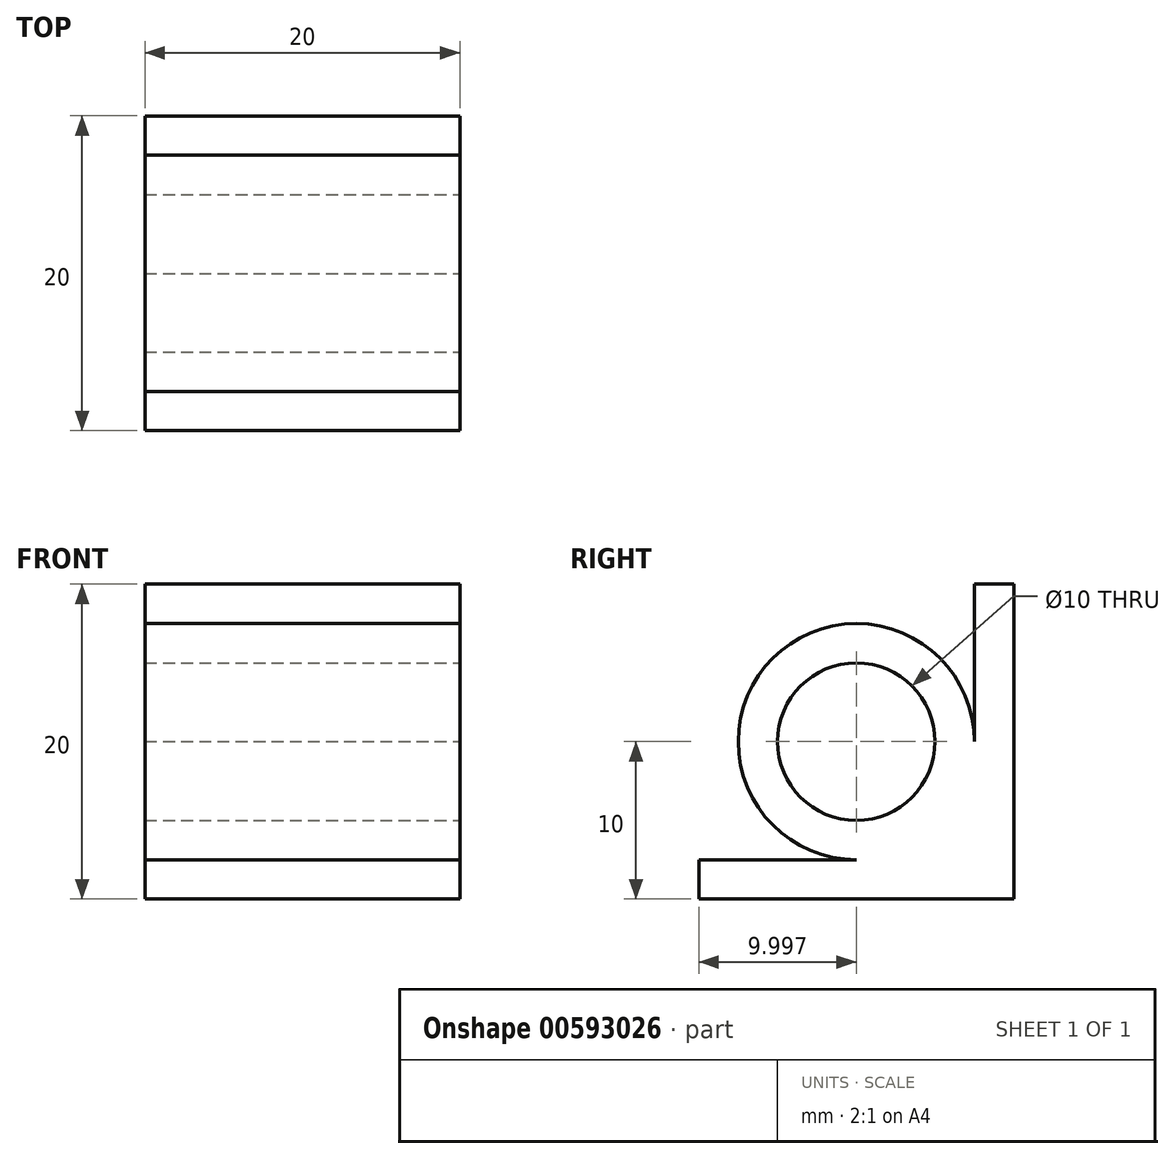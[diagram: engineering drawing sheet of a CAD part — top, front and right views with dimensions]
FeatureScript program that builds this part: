
annotation { "Feature Type Name" : "Feature", "Feature Type Description" : "" }
export const myFeature = defineFeature(function(context is Context, id is Id, definition is map)
    precondition{}
    {
        {
            var Q0;
            Q0=qCreatedBy(makeId("Top.planeOp"),FACE);
            var sketch = newSketch(context, id + "F0", { "sketchPlane" : qUnion([Q0])});
            skLineSegment(sketch, "E0", {"start": v(-97.21, -75.5) * mm, "end": v(-97.21, -55.5) * mm});
            skLineSegment(sketch, "E1", {"start": v(-97.21, -75.5) * mm, "end": v(-77.21, -75.5) * mm});
            skLineSegment(sketch, "E2", {"start": v(-77.21, -75.5) * mm, "end": v(-77.21, -55.5) * mm});
            skLineSegment(sketch, "E3", {"start": v(-77.21, -55.5) * mm, "end": v(-97.21, -55.5) * mm});
            skSolve(sketch);
        }
        {
            var Q0;
            Q0 = qSketchRegion(id + "F0", true);
            var Q1;
            Q1 = qSketchRegion(id + "F3", true);
            var Q2;
            Q2 = qSketchRegion(id + "F2", true);
            extrude(context, id + "F1", {"entities" : qUnion([Q0, Q1, Q2]), "depth" : 20 * mm, "offsetDistance" : 25 * mm});
        }
        {
            var Q0;
            Q0=qCreatedBy(makeId("Top.planeOp"),FACE);
            var sketch = newSketch(context, id + "F2", { "sketchPlane" : qUnion([Q0])});
            skSolve(sketch);
        }
        {
            var Q0;
            Q0=makeQuery(id+"F1.opExtrude","SWEPT_FACE",FACE,{"disambiguationData":[OSD([sQuery(id+"F0.wireOp",EDGE,"E2")])]});
            var sketch = newSketch(context, id + "F3", { "sketchPlane" : qUnion([Q0])});
            skLineSegment(sketch, "E4", {"start": v(-75.5, 20) * mm, "end": v(-55.5, 0) * mm});
            skLineSegment(sketch, "E5", {"start": v(-55.5, 20) * mm, "end": v(-75.5, 0) * mm});
            skCircle(sketch, "E6", {"center": v(-65.5, 10) * mm, "radius": 5 * mm});
            skSolve(sketch);
        }
        {
            var Q0;
            Q0=sQuery(id+"F3.wireOp",VERTEX,"E6.center");
            var Q1;
            Q1=makeQuery(id+"F1.opExtrude","SWEPT_BODY",BODY,{"disambiguationData":[OSD([sQuery(id+"F0.wireOp",EDGE,"E0"),sQuery(id+"F0.wireOp",EDGE,"E1"),sQuery(id+"F0.wireOp",EDGE,"E2"),sQuery(id+"F0.wireOp",EDGE,"E3")])]});
            hole(context, id + "F4", {"style" : HoleStyle.SIMPLE, "endStyle" : HoleEndStyle.THROUGH, "holeDiameter" : 10 * mm, "majorDiameter" : 5 * mm, "isTappedThrough" : true, "tappedDepth" : 12 * mm, "tapClearance" : 3, "locations" : qUnion([Q0]), "scope" : qUnion([Q1])});
        }
        {
            var Q0;
            Q0=makeQuery(id+"F1.opExtrude","SWEPT_FACE",FACE,{"disambiguationData":[OSD([sQuery(id+"F0.wireOp",EDGE,"E1")])]});
            var Q1;
            Q1=makeQuery(id+"F1.opExtrude","CAP_FACE",FACE,{"disambiguationData":[OSD([sQuery(id+"F0.wireOp",EDGE,"E0"),sQuery(id+"F0.wireOp",EDGE,"E1"),sQuery(id+"F0.wireOp",EDGE,"E2"),sQuery(id+"F0.wireOp",EDGE,"E3")])],"isStart":false});
            var Q2;
            Q2=makeQuery(id+"F1.opExtrude","SWEPT_FACE",FACE,{"disambiguationData":[OSD([sQuery(id+"F0.wireOp",EDGE,"E2")])]});
            var Q3;
            Q3=makeQuery(id+"F1.opExtrude","SWEPT_FACE",FACE,{"disambiguationData":[OSD([sQuery(id+"F0.wireOp",EDGE,"E0")])]});
            shell(context, id + "F5", {"entities" : qUnion([Q0, Q1, Q2, Q3]), "thickness" : 2.5 * mm});
        }
    });
